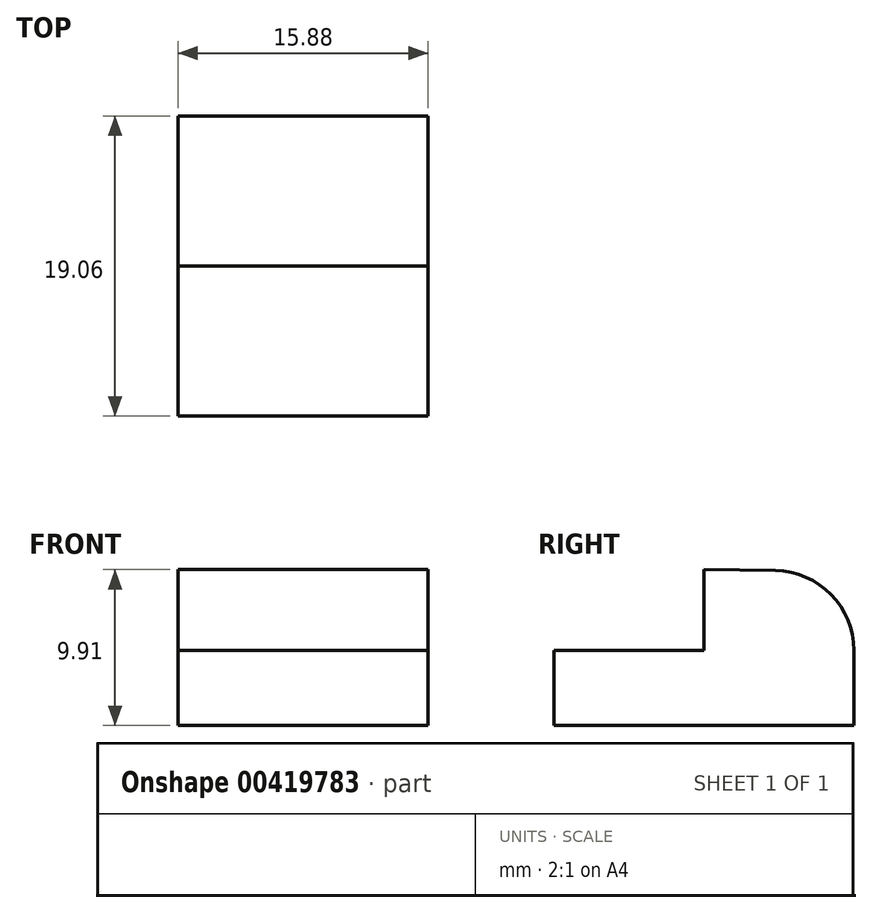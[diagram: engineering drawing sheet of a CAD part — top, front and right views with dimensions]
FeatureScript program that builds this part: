
annotation { "Feature Type Name" : "Feature", "Feature Type Description" : "" }
export const myFeature = defineFeature(function(context is Context, id is Id, definition is map)
    precondition{}
    {
        {
            var Q0;
            Q0=qCreatedBy(makeId("Right.planeOp"),FACE);
            var sketch = newSketch(context, id + "F0", { "sketchPlane" : qUnion([Q0])});
            skLineSegment(sketch, "E0.bottom", {"start": v(9.53, 2.38) * mm, "end": v(-9.53, 2.38) * mm});
            skLineSegment(sketch, "E0.top", {"start": v(9.53, -2.38) * mm, "end": v(-9.53, -2.38) * mm});
            skLineSegment(sketch, "E0.left", {"start": v(9.53, 2.38) * mm, "end": v(9.53, -2.38) * mm});
            skLineSegment(sketch, "E0.right", {"start": v(-9.53, 2.38) * mm, "end": v(-9.53, -2.38) * mm});
            skPoint(sketch, "E0.middle", {"position": v(0, 0) * mm});
            skArc(sketch, "E1", {"start": v(9.53, 2.38) * mm, "mid": v(8.07, 5.94) * mm, "end": v(4.53, 7.46) * mm});
            skLineSegment(sketch, "E2", {"start": v(4.53, 7.46) * mm, "end": v(0, 7.53) * mm});
            skLineSegment(sketch, "E3", {"start": v(0, 7.53) * mm, "end": v(0, 2.38) * mm});
            skSolve(sketch);
        }
        {
            var Q0;
            Q0=makeQuery(id+"F0.imprint","IMPRINT",FACE,{"disambiguationData":[TD([[makeQuery(id+"F0.imprint","IMPRINT",EDGE,{"derivedFrom":sQuery(id+"F0.wireOp",EDGE,"E0.top")}),-1.0]])]});
            var Q1;
            {var subQ0=sQuery(id+"F0.wireOp",EDGE,"E1");Q1=makeQuery(id+"F0.imprint","IMPRINT",FACE,{"disambiguationData":[TD([[makeQuery(id+"F0.imprint","IMPRINT",EDGE,{"derivedFrom":subQ0}),1.0]])]});}
            extrude(context, id + "F1", {"entities" : qUnion([Q0, Q1]), "endBound" : BoundingType.SYMMETRIC, "depth" : 15.88 * mm});
        }
    });
